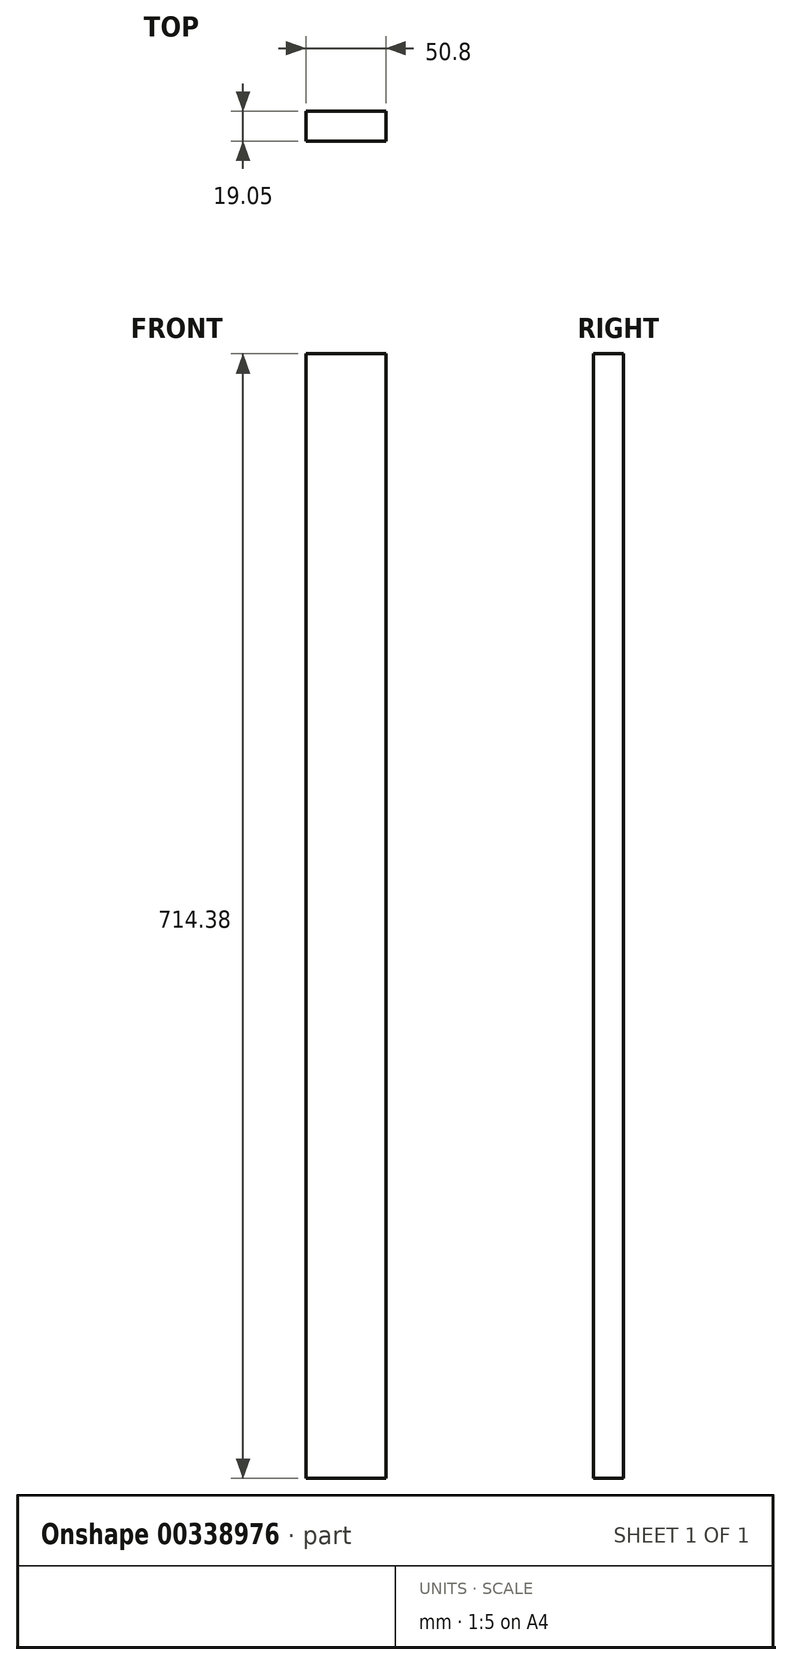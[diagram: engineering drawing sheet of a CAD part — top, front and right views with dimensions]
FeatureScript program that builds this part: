
annotation { "Feature Type Name" : "Feature", "Feature Type Description" : "" }
export const myFeature = defineFeature(function(context is Context, id is Id, definition is map)
    precondition{}
    {
        {
            var Q0;
            Q0=qCreatedBy(makeId("Front.planeOp"),FACE);
            var sketch = newSketch(context, id + "F0", { "sketchPlane" : qUnion([Q0])});
            skLineSegment(sketch, "E0.bottom", {"start": v(25.4, 357.19) * mm, "end": v(-25.4, 357.19) * mm});
            skLineSegment(sketch, "E0.top", {"start": v(25.4, -357.19) * mm, "end": v(-25.4, -357.19) * mm});
            skLineSegment(sketch, "E0.left", {"start": v(25.4, 357.19) * mm, "end": v(25.4, -357.19) * mm});
            skLineSegment(sketch, "E0.right", {"start": v(-25.4, 357.19) * mm, "end": v(-25.4, -357.19) * mm});
            skPoint(sketch, "E0.middle", {"position": v(0, 0) * mm});
            skSolve(sketch);
        }
        {
            var Q0;
            Q0 = qSketchRegion(id + "F0", true);
            extrude(context, id + "F1", {"entities" : qUnion([Q0]), "depth" : 19.05 * mm});
        }
    });
